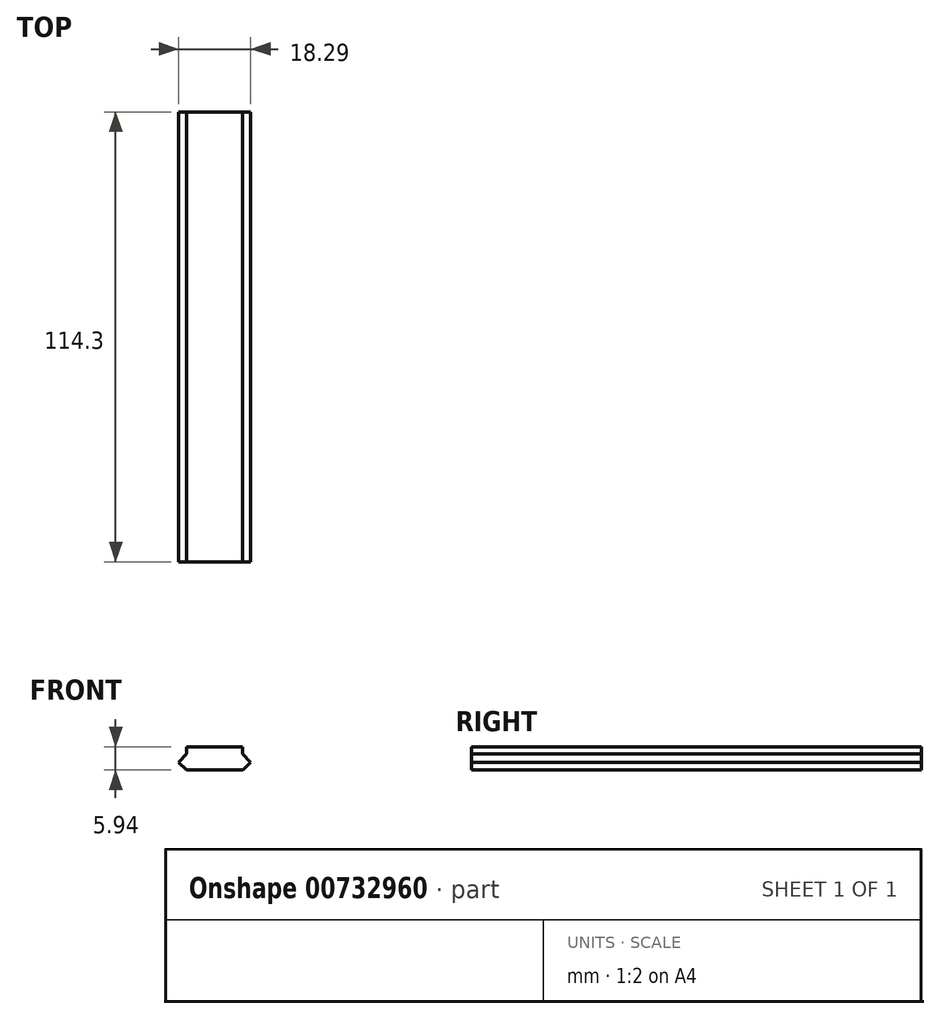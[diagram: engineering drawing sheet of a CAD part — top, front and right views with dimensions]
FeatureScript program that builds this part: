
annotation { "Feature Type Name" : "Feature", "Feature Type Description" : "" }
export const myFeature = defineFeature(function(context is Context, id is Id, definition is map)
    precondition{}
    {
        {
            var Q0;
            Q0=qCreatedBy(makeId("Front.planeOp"),FACE);
            var sketch = newSketch(context, id + "F0", { "sketchPlane" : qUnion([Q0])});
            skLineSegment(sketch, "E0", {"start": v(-17.1, 12.8) * mm, "end": v(1.18, 12.8) * mm});
            skLineSegment(sketch, "E1", {"start": v(-17.1, 12.8) * mm, "end": v(-15.08, 12.8) * mm});
            skLineSegment(sketch, "E2", {"start": v(-17.1, 12.8) * mm, "end": v(-15.08, 14.84) * mm});
            skLineSegment(sketch, "E3", {"start": v(-15.08, 14.84) * mm, "end": v(-15.08, 12.8) * mm});
            skLineSegment(sketch, "E4", {"start": v(-17.1, 12.8) * mm, "end": v(-15.08, 10.8) * mm});
            skLineSegment(sketch, "E5", {"start": v(-15.08, 10.8) * mm, "end": v(-15.08, 12.8) * mm});
            skLineSegment(sketch, "E6", {"start": v(1.18, 12.8) * mm, "end": v(-0.86, 12.8) * mm});
            skLineSegment(sketch, "E7", {"start": v(-0.86, 12.8) * mm, "end": v(-0.86, 14.84) * mm});
            skLineSegment(sketch, "E8", {"start": v(-0.86, 14.84) * mm, "end": v(1.18, 12.8) * mm});
            skLineSegment(sketch, "E9", {"start": v(1.18, 12.8) * mm, "end": v(-0.83, 10.8) * mm});
            skLineSegment(sketch, "E10", {"start": v(-0.83, 10.8) * mm, "end": v(-0.86, 12.8) * mm});
            skLineSegment(sketch, "E11", {"start": v(-15.08, 14.84) * mm, "end": v(-0.86, 14.84) * mm});
            skLineSegment(sketch, "E12", {"start": v(-15.08, 10.8) * mm, "end": v(-0.83, 10.8) * mm});
            skLineSegment(sketch, "E13", {"start": v(-15.08, 14.84) * mm, "end": v(-15.08, 16.73) * mm});
            skLineSegment(sketch, "E14", {"start": v(-15.08, 16.73) * mm, "end": v(-0.86, 16.73) * mm});
            skLineSegment(sketch, "E15", {"start": v(-0.86, 16.73) * mm, "end": v(-0.86, 14.84) * mm});
            skSolve(sketch);
        }
        {
            var Q0;
            Q0=makeQuery(id+"F0.imprint","IMPRINT",FACE,{"disambiguationData":[TD([[makeQuery(id+"F0.imprint","IMPRINT",EDGE,{"derivedFrom":sQuery(id+"F0.wireOp",EDGE,"E11")}),1.0]])]});
            var Q1;
            {var subQ2=sQuery(id+"F0.wireOp",EDGE,"E2");Q1=makeQuery(id+"F0.imprint","IMPRINT",FACE,{"disambiguationData":[TD([[makeQuery(id+"F0.imprint","IMPRINT",EDGE,{"derivedFrom":subQ2}),-1.0]])]});}
            var Q2;
            {var subQ2=sQuery(id+"F0.wireOp",EDGE,"E4");Q2=makeQuery(id+"F0.imprint","IMPRINT",FACE,{"disambiguationData":[TD([[makeQuery(id+"F0.imprint","IMPRINT",EDGE,{"derivedFrom":subQ2}),1.0]])]});}
            var Q3;
            {var subQ0=sQuery(id+"F0.wireOp",EDGE,"E7");Q3=makeQuery(id+"F0.imprint","IMPRINT",FACE,{"disambiguationData":[TD([[makeQuery(id+"F0.imprint","IMPRINT",EDGE,{"derivedFrom":subQ0}),-1.0]])]});}
            var Q4;
            {var subQ2=sQuery(id+"F0.wireOp",EDGE,"E9");Q4=makeQuery(id+"F0.imprint","IMPRINT",FACE,{"disambiguationData":[TD([[makeQuery(id+"F0.imprint","IMPRINT",EDGE,{"derivedFrom":subQ2}),-1.0]])]});}
            var Q5;
            {var subQ0=sQuery(id+"F0.wireOp",EDGE,"E5");Q5=makeQuery(id+"F0.imprint","IMPRINT",FACE,{"disambiguationData":[TD([[makeQuery(id+"F0.imprint","IMPRINT",EDGE,{"derivedFrom":subQ0}),-1.0]])]});}
            var Q6;
            {var subQ0=sQuery(id+"F0.wireOp",EDGE,"E3");Q6=makeQuery(id+"F0.imprint","IMPRINT",FACE,{"disambiguationData":[TD([[makeQuery(id+"F0.imprint","IMPRINT",EDGE,{"derivedFrom":subQ0}),1.0]])]});}
            extrude(context, id + "F1", {"entities" : qUnion([Q0, Q1, Q2, Q3, Q4, Q5, Q6]), "depth" : 114.3 * mm, "offsetDistance" : 25.4 * mm});
        }
    });
